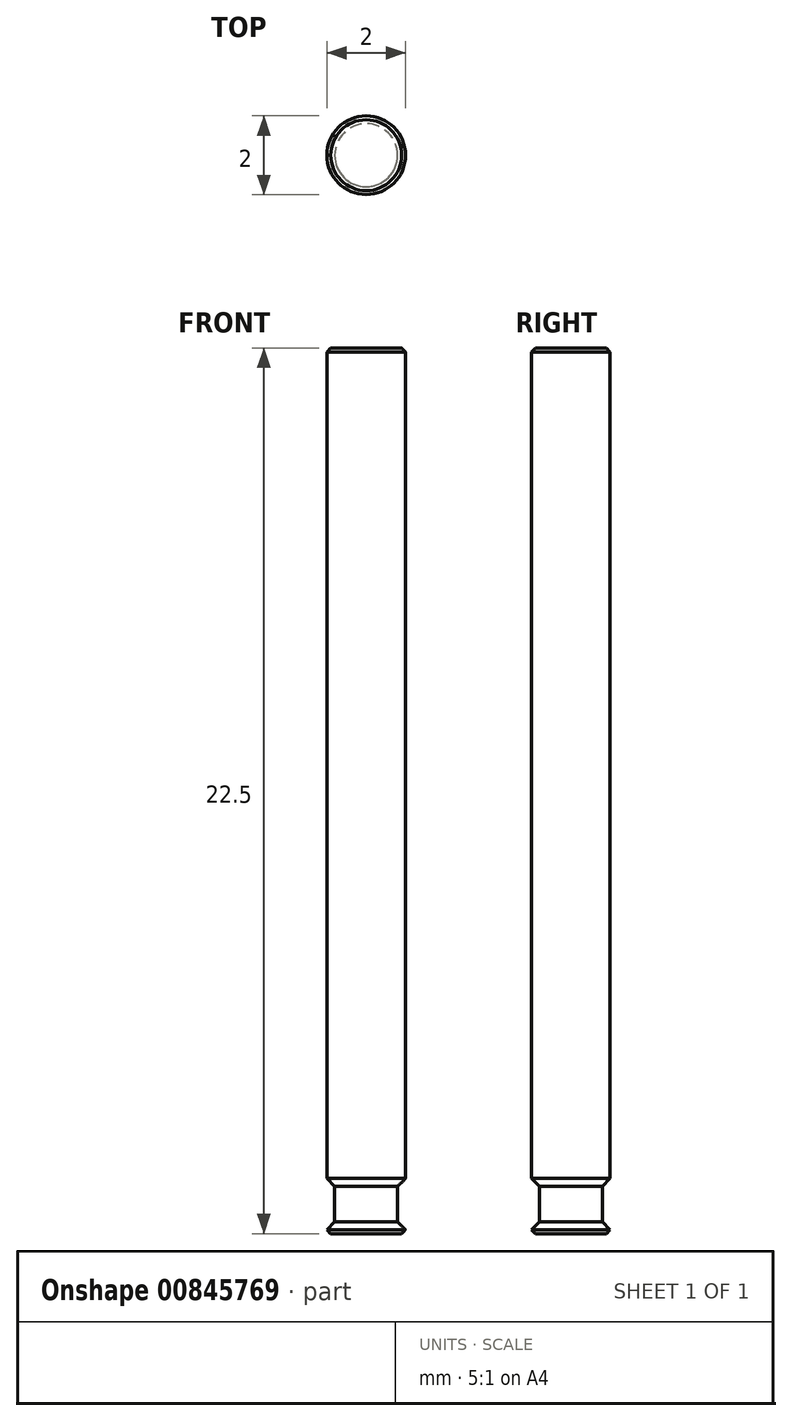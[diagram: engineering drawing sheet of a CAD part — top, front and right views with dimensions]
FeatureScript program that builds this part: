
annotation { "Feature Type Name" : "Feature", "Feature Type Description" : "" }
export const myFeature = defineFeature(function(context is Context, id is Id, definition is map)
    precondition{}
    {
        {
            var Q0;
            Q0=qCreatedBy(makeId("Top.planeOp"),FACE);
            var sketch = newSketch(context, id + "F0", { "sketchPlane" : qUnion([Q0])});
            skCircle(sketch, "E0", {"center": v(0, 0) * mm, "radius": 1 * mm});
            skSolve(sketch);
        }
        {
            var Q0;
            Q0 = qSketchRegion(id + "F0", true);
            extrude(context, id + "F1", {"entities" : qUnion([Q0]), "depth" : 22.5 * mm, "offsetDistance" : 25 * mm});
        }
        {
            var Q0;
            Q0=makeQuery(id+"F1.opExtrude","CAP_EDGE",EDGE,{"disambiguationData":[OSD([sQuery(id+"F0.wireOp",EDGE,"E0")])],"isStart":false});
            var Q1;
            Q1=makeQuery(id+"F1.opExtrude","CAP_EDGE",EDGE,{"disambiguationData":[OSD([sQuery(id+"F0.wireOp",EDGE,"E0")])],"isStart":true});
            chamfer(context, id + "F2", {"entities" : qUnion([Q0, Q1]), "width" : .1 * mm, "tangentPropagation" : true});
        }
        {
            var Q0;
            Q0=qCreatedBy(makeId("Right.planeOp"),FACE);
            var sketch = newSketch(context, id + "F3", { "sketchPlane" : qUnion([Q0])});
            skLineSegment(sketch, "E1.bottom", {"start": v(1.2, 0.5) * mm, "end": v(0.8, 0.5) * mm});
            skLineSegment(sketch, "E1.top", {"start": v(1.2, 1) * mm, "end": v(0.8, 1) * mm});
            skLineSegment(sketch, "E1.left", {"start": v(1.2, 0.5) * mm, "end": v(1.2, 1) * mm});
            skLineSegment(sketch, "E1.right", {"start": v(0.8, 0.5) * mm, "end": v(0.8, 1) * mm});
            skSolve(sketch);
        }
        {
            var Q0;
            Q0=makeQuery(id+"F3.imprint","IMPRINT",FACE,{"disambiguationData":[TD([[makeQuery(id+"F3.imprint","IMPRINT",EDGE,{"derivedFrom":sQuery(id+"F3.wireOp",EDGE,"E1.bottom")}),-1.0]])]});
            var Q1;
            {var subQ0=sQuery(id+"F0.wireOp",EDGE,"E0");Q1=makeQuery(id+"F2.opChamfer","BLEND_EDGE",EDGE,{"blendedFrom":[makeQuery(id+"F1.opExtrude","CAP_EDGE",EDGE,{"disambiguationData":[OSD([subQ0])],"isStart":true}),makeQuery(id+"F1.opExtrude","CAP_FACE",FACE,{"disambiguationData":[OSD([subQ0])],"isStart":true})],"blendedInto":[makeQuery(id+"F1.opExtrude","CAP_FACE",FACE,{"disambiguationData":[OSD([subQ0])],"isStart":true})]});}
            revolve(context, id + "F4", {"operationType" : NewBodyOperationType.REMOVE, "surfaceOperationType" : NewSurfaceOperationType.NEW, "entities" : qUnion([Q0]), "axis" : qUnion([Q1]), "revolveType" : RevolveType.FULL, "oppositeDirection" : true});
        }
        {
            var Q0;
            Q0=makeQuery(id+"F4.boolean.opBoolean","INTERSECT",EDGE,{"derivedFrom":[makeQuery(id+"F1.opExtrude","SWEPT_FACE",FACE,{"disambiguationData":[OSD([sQuery(id+"F0.wireOp",EDGE,"E0")])]}),makeQuery(id+"F4.opRevolve","SWEPT_FACE",FACE,{"disambiguationData":[OSD([sQuery(id+"F3.wireOp",EDGE,"E1.bottom")])]})]});
            var Q1;
            Q1=makeQuery(id+"F4.boolean.opBoolean","INTERSECT",EDGE,{"derivedFrom":[makeQuery(id+"F1.opExtrude","SWEPT_FACE",FACE,{"disambiguationData":[OSD([sQuery(id+"F0.wireOp",EDGE,"E0")])]}),makeQuery(id+"F4.opRevolve","SWEPT_FACE",FACE,{"disambiguationData":[OSD([sQuery(id+"F3.wireOp",EDGE,"E1.top")])]})]});
            chamfer(context, id + "F5", {"entities" : qUnion([Q0, Q1]), "width" : .4 * mm, "tangentPropagation" : true});
        }
    });
